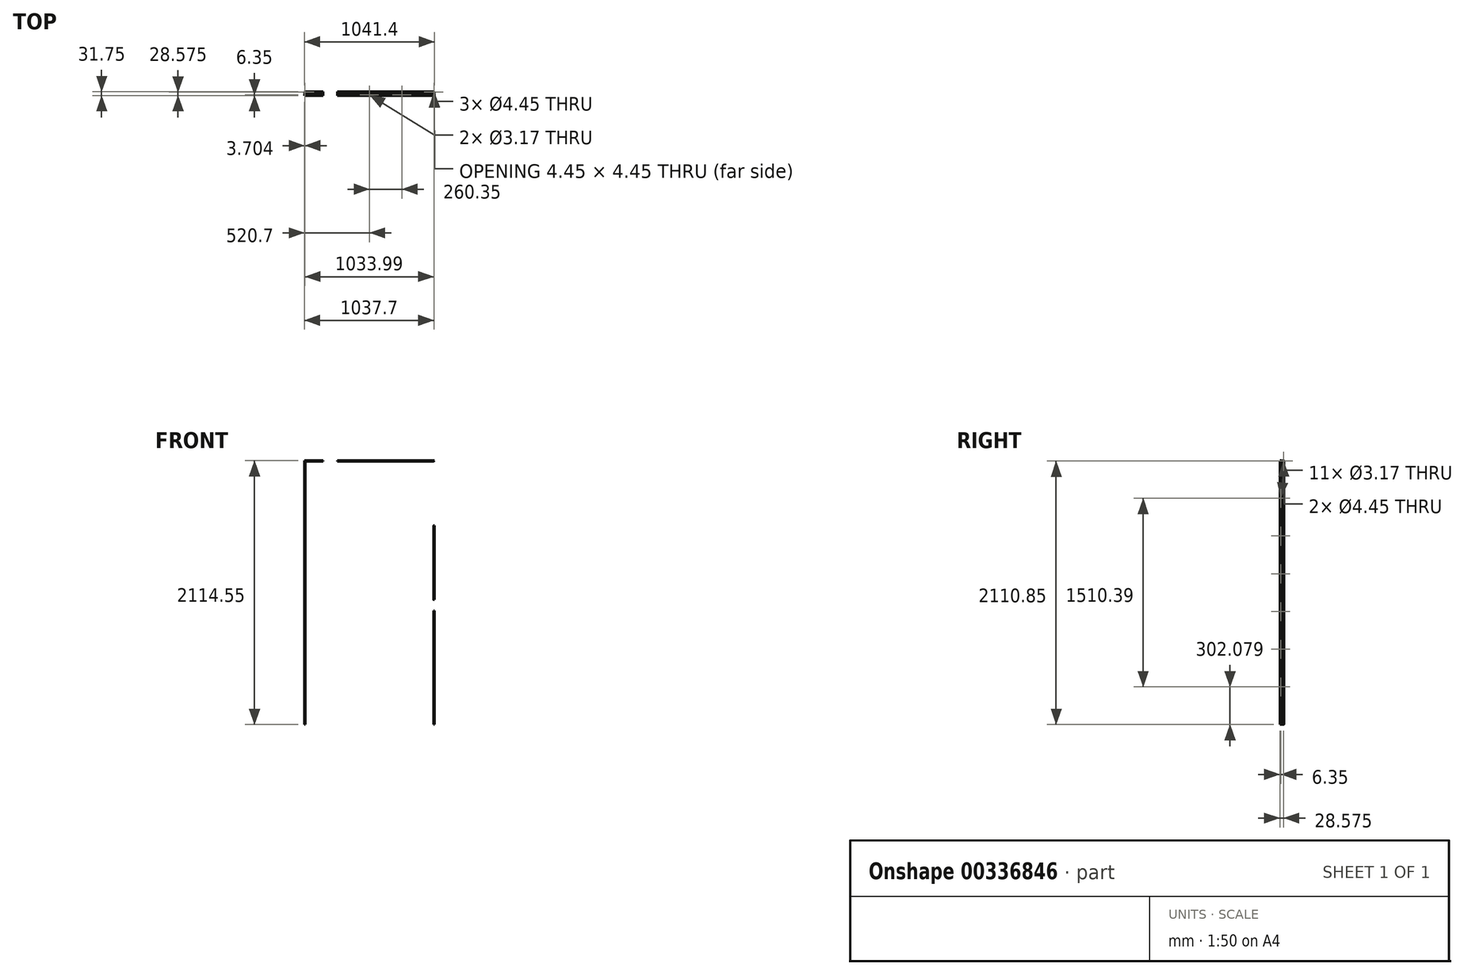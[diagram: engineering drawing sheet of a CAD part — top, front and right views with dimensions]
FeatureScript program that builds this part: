
annotation { "Feature Type Name" : "Feature", "Feature Type Description" : "" }
export const myFeature = defineFeature(function(context is Context, id is Id, definition is map)
    precondition{}
    {
        {
            var Q0;
            Q0=qCreatedBy(makeId("Top.planeOp"),FACE);
            var sketch = newSketch(context, id + "F0", { "sketchPlane" : qUnion([Q0])});
            skLineSegment(sketch, "E0", {"start": v(0, 0) * mm, "end": v(-1.06, 0) * mm});
            skLineSegment(sketch, "E1", {"start": v(-1.06, 0) * mm, "end": v(-1.06, 12.29) * mm});
            skLineSegment(sketch, "E2", {"start": v(-1.06, 12.29) * mm, "end": v(-6.35, 18) * mm});
            skLineSegment(sketch, "E3", {"start": v(-6.35, 18) * mm, "end": v(-6.35, 24.13) * mm});
            skLineSegment(sketch, "E4", {"start": v(-6.35, 24.13) * mm, "end": v(-5.3, 25.4) * mm});
            skLineSegment(sketch, "E5", {"start": v(-5.3, 25.4) * mm, "end": v(-5.3, 23.42) * mm});
            skLineSegment(sketch, "E6", {"start": v(-5.3, 23.42) * mm, "end": v(-4.23, 23.42) * mm});
            skLineSegment(sketch, "E7", {"start": v(-4.23, 23.42) * mm, "end": v(-4.23, 21.45) * mm});
            skLineSegment(sketch, "E8", {"start": v(-4.23, 21.45) * mm, "end": v(-5.3, 21.45) * mm});
            skLineSegment(sketch, "E9", {"start": v(-5.3, 21.45) * mm, "end": v(-5.3, 19.47) * mm});
            skLineSegment(sketch, "E10", {"start": v(-5.3, 19.47) * mm, "end": v(-2.12, 19.47) * mm});
            skLineSegment(sketch, "E11", {"start": v(-2.12, 19.47) * mm, "end": v(-2.12, 21.45) * mm});
            skLineSegment(sketch, "E12", {"start": v(-2.12, 21.45) * mm, "end": v(-3.18, 21.45) * mm});
            skLineSegment(sketch, "E13", {"start": v(-3.17, 21.45) * mm, "end": v(-3.17, 23.42) * mm});
            skLineSegment(sketch, "E14", {"start": v(-3.17, 23.42) * mm, "end": v(-2.12, 23.42) * mm});
            skLineSegment(sketch, "E15", {"start": v(-2.12, 23.42) * mm, "end": v(-2.12, 25.4) * mm});
            skLineSegment(sketch, "E16", {"start": v(-2.12, 25.4) * mm, "end": v(-1.06, 24.13) * mm});
            skLineSegment(sketch, "E17", {"start": v(-1.06, 24.13) * mm, "end": v(-1.06, 26.2) * mm});
            skLineSegment(sketch, "E18", {"start": v(-1.06, 26.2) * mm, "end": v(0, 26.2) * mm});
            skLineSegment(sketch, "E19", {"start": v(-5.3, 19.47) * mm, "end": v(-6.35, 19.47) * mm, "construction": true});
            skLineSegment(sketch, "E20", {"start": v(-2.12, 23.42) * mm, "end": v(-1.06, 23.42) * mm, "construction": true});
            skLineSegment(sketch, "E21", {"start": v(-3.17, 22.44) * mm, "end": v(-4.23, 22.44) * mm, "construction": true});
            skLineSegment(sketch, "E22", {"start": v(-1.06, 8.25) * mm, "end": v(0, 8.25) * mm, "construction": true});
            skLineSegment(sketch, "E23.0", {"start": v(0, 12.7) * mm, "end": v(-5.3, 18.41) * mm});
            skLineSegment(sketch, "E23.1", {"start": v(0, 0) * mm, "end": v(0, 12.7) * mm});
            skLineSegment(sketch, "E24", {"start": v(0, 26.2) * mm, "end": v(0, 18.41) * mm});
            skLineSegment(sketch, "E25", {"start": v(0, 18.41) * mm, "end": v(-5.3, 18.41) * mm});
            skLineSegment(sketch, "E26", {"start": v(-2.69, 19.47) * mm, "end": v(-2.69, 18.41) * mm, "construction": true});
            skSolve(sketch);
        }
        {
            var Q0;
            Q0=qCreatedBy(makeId("Top.planeOp"),FACE);
            var sketch = newSketch(context, id + "F1", { "sketchPlane" : qUnion([Q0])});
            skLineSegment(sketch, "E27.0", {"start": v(-3.18, 23.42) * mm, "end": v(-2.12, 23.42) * mm});
            skLineSegment(sketch, "E28.0", {"start": v(-3.17, 21.45) * mm, "end": v(-3.17, 23.42) * mm});
            skLineSegment(sketch, "E29.0", {"start": v(-4.23, 23.42) * mm, "end": v(-4.23, 21.45) * mm});
            skLineSegment(sketch, "E30.0", {"start": v(-5.3, 23.42) * mm, "end": v(-4.23, 23.42) * mm});
            skLineSegment(sketch, "E31.0", {"start": v(-4.23, 21.45) * mm, "end": v(-5.3, 21.45) * mm});
            skLineSegment(sketch, "E32.0", {"start": v(-5.3, 21.45) * mm, "end": v(-5.3, 19.47) * mm});
            skLineSegment(sketch, "E33.0", {"start": v(-2.12, 21.45) * mm, "end": v(-3.18, 21.45) * mm});
            skLineSegment(sketch, "E34.0", {"start": v(-2.12, 19.47) * mm, "end": v(-2.12, 21.45) * mm});
            skLineSegment(sketch, "E35.0", {"start": v(-5.3, 19.47) * mm, "end": v(-2.12, 19.47) * mm});
            skLineSegment(sketch, "E36", {"start": v(-2.12, 25.4) * mm, "end": v(-5.3, 25.4) * mm, "construction": true});
            skLineSegment(sketch, "E37", {"start": v(-3.7, 25.4) * mm, "end": v(-3.7, 28.57) * mm, "construction": true});
            skPoint(sketch, "E37.endSnap0", {"position": v(-3.7, 25.4) * mm});
            skCircle(sketch, "E38", {"center": v(-3.7, 28.57) * mm, "radius": 3.18 * mm, "construction": true});
            skLineSegment(sketch, "E39", {"start": v(-2.12, 23.42) * mm, "end": v(-2.12, 25.83) * mm});
            skLineSegment(sketch, "E40", {"start": v(-5.3, 23.42) * mm, "end": v(-5.3, 25.83) * mm});
            skArc(sketch, "E41", {"start": v(-5.3, 25.83) * mm, "mid": v(-3.7, 31.75) * mm, "end": v(-2.12, 25.83) * mm});
            skCircle(sketch, "E42", {"center": v(-3.7, 28.57) * mm, "radius": 2.22 * mm});
            skSolve(sketch);
        }
        {
            var Q0;
            Q0=makeQuery(id+"F1.imprint","IMPRINT",FACE,{"disambiguationData":[TD([[makeQuery(id+"F1.imprint","IMPRINT",EDGE,{"derivedFrom":sQuery(id+"F1.wireOp",EDGE,"E27.0")}),1.0]])]});
            extrude(context, id + "F2", {"entities" : qUnion([Q0]), "depth" : 2114.55 * mm});
        }
        {
            var Q0;
            Q0=makeQuery(id+"F0.imprint","IMPRINT",FACE,{"disambiguationData":[TD([[makeQuery(id+"F0.imprint","IMPRINT",EDGE,{"derivedFrom":sQuery(id+"F0.wireOp",EDGE,"E0")}),-1.0]])]});
            extrude(context, id + "F3", {"entities" : qUnion([Q0]), "depth" : 2114.55 * mm});
        }
        {
            var Q0;
            Q0=qCreatedBy(makeId("Top.planeOp"),FACE);
            var sketch = newSketch(context, id + "F4", { "sketchPlane" : qUnion([Q0])});
            skPoint(sketch, "E43", {"position": v(-520.7, 0) * mm});
            skSolve(sketch);
        }
        {
            var Q0;
            Q0=qCreatedBy(makeId("Right.planeOp"),FACE);
            var Q1;
            Q1=sQuery(id+"F4.wireOp",VERTEX,"E43");
            cPlane(context, id + "F5", {"entities" : qUnion([Q0, Q1]), "cplaneType" : CPlaneType.PLANE_POINT, "offset" : 25.4 * mm, "width" : 152.4 * mm, "height" : 152.4 * mm});
        }
        {
            var Q0;
            Q0=makeQuery(id+"F2.opExtrude","SWEPT_BODY",BODY,{"disambiguationData":[OSD([sQuery(id+"F1.wireOp",EDGE,"E27.0"),sQuery(id+"F1.wireOp",EDGE,"E28.0"),sQuery(id+"F1.wireOp",EDGE,"E29.0"),sQuery(id+"F1.wireOp",EDGE,"E30.0"),sQuery(id+"F1.wireOp",EDGE,"E31.0"),sQuery(id+"F1.wireOp",EDGE,"E32.0"),sQuery(id+"F1.wireOp",EDGE,"E33.0"),sQuery(id+"F1.wireOp",EDGE,"E34.0"),sQuery(id+"F1.wireOp",EDGE,"E35.0"),sQuery(id+"F1.wireOp",EDGE,"E39"),sQuery(id+"F1.wireOp",EDGE,"E40"),sQuery(id+"F1.wireOp",EDGE,"E41"),sQuery(id+"F1.wireOp",EDGE,"E42")])]});
            var Q1;
            Q1=makeQuery(id+"F3.opExtrude","SWEPT_BODY",BODY,{"disambiguationData":[OSD([sQuery(id+"F0.wireOp",EDGE,"E0"),sQuery(id+"F0.wireOp",EDGE,"E1"),sQuery(id+"F0.wireOp",EDGE,"E2"),sQuery(id+"F0.wireOp",EDGE,"E3"),sQuery(id+"F0.wireOp",EDGE,"E4"),sQuery(id+"F0.wireOp",EDGE,"E5"),sQuery(id+"F0.wireOp",EDGE,"E6"),sQuery(id+"F0.wireOp",EDGE,"E7"),sQuery(id+"F0.wireOp",EDGE,"E8"),sQuery(id+"F0.wireOp",EDGE,"E9"),sQuery(id+"F0.wireOp",EDGE,"E10"),sQuery(id+"F0.wireOp",EDGE,"E11"),sQuery(id+"F0.wireOp",EDGE,"E12"),sQuery(id+"F0.wireOp",EDGE,"E13"),sQuery(id+"F0.wireOp",EDGE,"E14"),sQuery(id+"F0.wireOp",EDGE,"E15"),sQuery(id+"F0.wireOp",EDGE,"E16"),sQuery(id+"F0.wireOp",EDGE,"E17"),sQuery(id+"F0.wireOp",EDGE,"E18"),sQuery(id+"F0.wireOp",EDGE,"E23.0"),sQuery(id+"F0.wireOp",EDGE,"E23.1"),sQuery(id+"F0.wireOp",EDGE,"E24"),sQuery(id+"F0.wireOp",EDGE,"E25")])]});
            var Q2;
            Q2=qCreatedBy(id+"F5.planeOp",FACE);
            mirror(context, id + "F6", {"entities" : qUnion([Q0, Q1]), "mirrorPlane" : qUnion([Q2])});
        }
        {
            var Q0;
            Q0=qCreatedBy(makeId("Front.planeOp"),FACE);
            var sketch = newSketch(context, id + "F7", { "sketchPlane" : qUnion([Q0])});
            skPoint(sketch, "E44.0", {"position": v(-1041.4, 2114.55) * mm});
            skPoint(sketch, "E45.0", {"position": v(0, 2114.55) * mm});
            skLineSegment(sketch, "E46", {"start": v(-1041.4, 2114.55) * mm, "end": v(-520.7, 1593.85) * mm});
            skLineSegment(sketch, "E47", {"start": v(-520.7, 1593.85) * mm, "end": v(0, 2114.55) * mm});
            skLineSegment(sketch, "E48", {"start": v(-1041.4, 2114.55) * mm, "end": v(0, 2114.55) * mm});
            skSolve(sketch);
        }
        {
            var Q0;
            Q0 = qSketchRegion(id + "F7", true);
            extrude(context, id + "F8", {"entities" : qUnion([Q0]), "operationType" : NewBodyOperationType.REMOVE, "endBound" : BoundingType.THROUGH_ALL, "oppositeDirection" : true, "depth" : 25.4 * mm, "hasSecondDirection" : true, "secondDirectionBound" : SecondDirectionBoundingType.THROUGH_ALL, "secondDirectionOppositeDirection" : false, "secondDirectionDepth" : 25.4 * mm});
        }
        {
            var Q0;
            Q0=qCreatedBy(makeId("Top.planeOp"),FACE);
            var Q1;
            Q1=sQuery(id+"F7.wireOp",VERTEX,"E47.start");
            cPlane(context, id + "F9", {"entities" : qUnion([Q0, Q1]), "cplaneType" : CPlaneType.PLANE_POINT, "offset" : 25.4 * mm, "width" : 152.4 * mm, "height" : 152.4 * mm});
        }
        {
            var Q0;
            Q0=qCreatedBy(id+"F9.planeOp",FACE);
            var sketch = newSketch(context, id + "F10", { "sketchPlane" : qUnion([Q0])});
            skPoint(sketch, "E49.0", {"position": v(-520.7, 0) * mm});
            skLineSegment(sketch, "E50", {"start": v(-520.7, 0) * mm, "end": v(-520.7, 397.43) * mm, "construction": true});
            skSolve(sketch);
        }
        {
            var Q0;
            Q0=makeQuery(id+"F2.opExtrude","SWEPT_BODY",BODY,{"disambiguationData":[OSD([sQuery(id+"F1.wireOp",EDGE,"E27.0"),sQuery(id+"F1.wireOp",EDGE,"E28.0"),sQuery(id+"F1.wireOp",EDGE,"E29.0"),sQuery(id+"F1.wireOp",EDGE,"E30.0"),sQuery(id+"F1.wireOp",EDGE,"E31.0"),sQuery(id+"F1.wireOp",EDGE,"E32.0"),sQuery(id+"F1.wireOp",EDGE,"E33.0"),sQuery(id+"F1.wireOp",EDGE,"E34.0"),sQuery(id+"F1.wireOp",EDGE,"E35.0"),sQuery(id+"F1.wireOp",EDGE,"E39"),sQuery(id+"F1.wireOp",EDGE,"E40"),sQuery(id+"F1.wireOp",EDGE,"E41"),sQuery(id+"F1.wireOp",EDGE,"E42")])]});
            var Q1;
            Q1=makeQuery(id+"F3.opExtrude","SWEPT_BODY",BODY,{"disambiguationData":[OSD([sQuery(id+"F0.wireOp",EDGE,"E0"),sQuery(id+"F0.wireOp",EDGE,"E1"),sQuery(id+"F0.wireOp",EDGE,"E2"),sQuery(id+"F0.wireOp",EDGE,"E3"),sQuery(id+"F0.wireOp",EDGE,"E4"),sQuery(id+"F0.wireOp",EDGE,"E5"),sQuery(id+"F0.wireOp",EDGE,"E6"),sQuery(id+"F0.wireOp",EDGE,"E7"),sQuery(id+"F0.wireOp",EDGE,"E8"),sQuery(id+"F0.wireOp",EDGE,"E9"),sQuery(id+"F0.wireOp",EDGE,"E10"),sQuery(id+"F0.wireOp",EDGE,"E11"),sQuery(id+"F0.wireOp",EDGE,"E12"),sQuery(id+"F0.wireOp",EDGE,"E13"),sQuery(id+"F0.wireOp",EDGE,"E14"),sQuery(id+"F0.wireOp",EDGE,"E15"),sQuery(id+"F0.wireOp",EDGE,"E16"),sQuery(id+"F0.wireOp",EDGE,"E17"),sQuery(id+"F0.wireOp",EDGE,"E18"),sQuery(id+"F0.wireOp",EDGE,"E23.0"),sQuery(id+"F0.wireOp",EDGE,"E23.1"),sQuery(id+"F0.wireOp",EDGE,"E24"),sQuery(id+"F0.wireOp",EDGE,"E25")])]});
            var Q2;
            Q2=sQuery(id+"F10.wireOp",EDGE,"E50");
            circularPattern(context, id + "F11", {"entities" : qUnion([Q0, Q1]), "axis" : qUnion([Q2]), "angle" : 270 * degree, "instanceCount" : 2, "equalSpace" : true});
        }
        {
            var Q0;
            Q0=qCreatedBy(makeId("Front.planeOp"),FACE);
            var sketch = newSketch(context, id + "F12", { "sketchPlane" : qUnion([Q0])});
            skPoint(sketch, "E51.0", {"position": v(0, 2114.55) * mm});
            skPoint(sketch, "E52.0", {"position": v(-520.7, 1593.85) * mm});
            skLineSegment(sketch, "E53", {"start": v(-520.7, 1593.85) * mm, "end": v(1152.4, 1593.85) * mm});
            skLineSegment(sketch, "E54", {"start": v(-520.7, 1593.85) * mm, "end": v(0, 2114.55) * mm});
            skLineSegment(sketch, "E55", {"start": v(0, 2114.55) * mm, "end": v(1152.4, 3266.95) * mm});
            skLineSegment(sketch, "E56", {"start": v(1152.4, 3266.95) * mm, "end": v(1152.4, 1593.85) * mm});
            skSolve(sketch);
        }
        {
            var Q0;
            Q0 = qSketchRegion(id + "F12", true);
            extrude(context, id + "F13", {"entities" : qUnion([Q0]), "operationType" : NewBodyOperationType.REMOVE, "endBound" : BoundingType.THROUGH_ALL, "depth" : 25.4 * mm, "hasSecondDirection" : true, "secondDirectionBound" : SecondDirectionBoundingType.THROUGH_ALL, "secondDirectionOppositeDirection" : true, "secondDirectionDepth" : 25.4 * mm});
        }
        {
            var Q0;
            Q0=qCreatedBy(makeId("Front.planeOp"),FACE);
            var sketch = newSketch(context, id + "F14", { "sketchPlane" : qUnion([Q0])});
            skLineSegment(sketch, "E57.bottom", {"start": v(-59.79, 999.28) * mm, "end": v(86.07, 999.28) * mm});
            skLineSegment(sketch, "E57.top", {"start": v(-59.79, 910.38) * mm, "end": v(86.07, 910.38) * mm});
            skLineSegment(sketch, "E57.left", {"start": v(-59.79, 999.28) * mm, "end": v(-59.79, 910.38) * mm});
            skLineSegment(sketch, "E57.right", {"start": v(86.07, 999.28) * mm, "end": v(86.07, 910.38) * mm});
            skSolve(sketch);
        }
        {
            var Q0;
            Q0 = qSketchRegion(id + "F14", true);
            extrude(context, id + "F15", {"entities" : qUnion([Q0]), "operationType" : NewBodyOperationType.REMOVE, "oppositeDirection" : true, "depth" : 60.96 * mm});
        }
        {
            var Q0;
            Q0=qCreatedBy(makeId("Right.planeOp"),FACE);
            var sketch = newSketch(context, id + "F16", { "sketchPlane" : qUnion([Q0])});
            skPoint(sketch, "E58.0", {"position": v(6.35, 0) * mm});
            skPoint(sketch, "E59.0", {"position": v(6.35, 2114.55) * mm});
            skLineSegment(sketch, "E60", {"start": v(6.35, 2114.55) * mm, "end": v(6.35, 1812.47) * mm, "construction": true});
            skLineSegment(sketch, "E61", {"start": v(6.35, 1812.47) * mm, "end": v(6.35, 1510.4) * mm, "construction": true});
            skLineSegment(sketch, "E62", {"start": v(6.35, 1510.4) * mm, "end": v(6.35, 1208.31) * mm, "construction": true});
            skLineSegment(sketch, "E63", {"start": v(6.35, 1208.31) * mm, "end": v(6.35, 906.24) * mm, "construction": true});
            skLineSegment(sketch, "E64", {"start": v(6.35, 906.24) * mm, "end": v(6.35, 604.16) * mm, "construction": true});
            skLineSegment(sketch, "E65", {"start": v(6.35, 604.16) * mm, "end": v(6.35, 302.08) * mm, "construction": true});
            skLineSegment(sketch, "E66", {"start": v(6.35, 302.08) * mm, "end": v(6.35, 0) * mm, "construction": true});
            skCircle(sketch, "E67", {"center": v(6.35, 1812.47) * mm, "radius": 1.59 * mm});
            skCircle(sketch, "E68", {"center": v(6.35, 1510.4) * mm, "radius": 1.59 * mm});
            skCircle(sketch, "E69", {"center": v(6.35, 1208.31) * mm, "radius": 1.59 * mm});
            skCircle(sketch, "E70", {"center": v(6.35, 906.24) * mm, "radius": 1.59 * mm});
            skCircle(sketch, "E71", {"center": v(6.35, 604.16) * mm, "radius": 1.59 * mm});
            skCircle(sketch, "E72", {"center": v(6.35, 302.08) * mm, "radius": 1.59 * mm});
            skSolve(sketch);
        }
        {
            var Q0;
            Q0 = qSketchRegion(id + "F16", true);
            extrude(context, id + "F17", {"entities" : qUnion([Q0]), "operationType" : NewBodyOperationType.REMOVE, "endBound" : BoundingType.THROUGH_ALL, "oppositeDirection" : true, "depth" : 25.4 * mm, "hasSecondDirection" : true, "secondDirectionBound" : SecondDirectionBoundingType.THROUGH_ALL, "secondDirectionOppositeDirection" : false, "secondDirectionDepth" : 25.4 * mm});
        }
        {
            var Q0;
            Q0=qCreatedBy(makeId("Top.planeOp"),FACE);
            var sketch = newSketch(context, id + "F18", { "sketchPlane" : qUnion([Q0])});
            skPoint(sketch, "E73.0", {"position": v(-1041.4, 6.35) * mm});
            skPoint(sketch, "E74.0", {"position": v(0, 6.35) * mm});
            skLineSegment(sketch, "E75", {"start": v(-1041.4, 6.35) * mm, "end": v(-781.05, 6.35) * mm, "construction": true});
            skLineSegment(sketch, "E76", {"start": v(-781.05, 6.35) * mm, "end": v(-520.7, 6.35) * mm, "construction": true});
            skLineSegment(sketch, "E77", {"start": v(-520.7, 6.35) * mm, "end": v(-260.35, 6.35) * mm, "construction": true});
            skLineSegment(sketch, "E78", {"start": v(-260.35, 6.35) * mm, "end": v(0, 6.35) * mm, "construction": true});
            skCircle(sketch, "E79", {"center": v(-781.05, 6.35) * mm, "radius": 1.59 * mm});
            skCircle(sketch, "E80", {"center": v(-520.7, 6.35) * mm, "radius": 1.59 * mm});
            skCircle(sketch, "E81", {"center": v(-260.35, 6.35) * mm, "radius": 1.59 * mm});
            skSolve(sketch);
        }
        {
            var Q0;
            Q0 = qSketchRegion(id + "F18", true);
            extrude(context, id + "F19", {"entities" : qUnion([Q0]), "operationType" : NewBodyOperationType.REMOVE, "endBound" : BoundingType.THROUGH_ALL, "oppositeDirection" : true, "depth" : 25.4 * mm, "hasSecondDirection" : true, "secondDirectionBound" : SecondDirectionBoundingType.THROUGH_ALL, "secondDirectionOppositeDirection" : false, "secondDirectionDepth" : 25.4 * mm});
        }
        {
            var Q0;
            Q0=qCreatedBy(makeId("Front.planeOp"),FACE);
            var sketch = newSketch(context, id + "F20", { "sketchPlane" : qUnion([Q0])});
            skLineSegment(sketch, "E82.bottom", {"start": v(-890.71, 2205.47) * mm, "end": v(-779.04, 2205.47) * mm});
            skLineSegment(sketch, "E82.top", {"start": v(-890.71, 2074.54) * mm, "end": v(-779.04, 2074.54) * mm});
            skLineSegment(sketch, "E82.left", {"start": v(-890.71, 2205.47) * mm, "end": v(-890.71, 2074.54) * mm});
            skLineSegment(sketch, "E82.right", {"start": v(-779.04, 2205.47) * mm, "end": v(-779.04, 2074.54) * mm});
            skSolve(sketch);
        }
        {
            var Q0;
            Q0 = qSketchRegion(id + "F20", true);
            extrude(context, id + "F21", {"entities" : qUnion([Q0]), "operationType" : NewBodyOperationType.REMOVE, "endBound" : BoundingType.THROUGH_ALL, "oppositeDirection" : true, "depth" : 25.4 * mm, "hasSecondDirection" : true, "secondDirectionBound" : SecondDirectionBoundingType.THROUGH_ALL, "secondDirectionOppositeDirection" : false, "secondDirectionDepth" : 25.4 * mm});
        }
    });
